# Revit family: Zumtobel CAELA
name_source: partatom
category: Lighting Fixtures
revit_build: Autodesk Revit 2018 (Build: 20170223_1515(x64)
units: mm (PartAtom-declared; Revit-internal decimal feet)

## family parameters
Cut with Voids When Loaded = No
Host = Face
Light Source = Yes
OmniClass Number = 23.80.70.11
OmniClass Title = Luminaries for Internal Lighting
Part Type = Normal
Room Calculation Point = No
Round Connector Dimension = Use Diameter
Shared = No

## types (4) — shared parameters
Assembly Code = D5020200
Color Filter = 16777215
Dimming Lamp Color Temperature Shift = <None>
Emit Shape Visible in Rendering = No
Height = 57 mm  [stored 0.187008 ft]
Lamp = LED
Manufacturer = Zumtobel Lighting
Tilt Angle = -90.00°
URL = http://www.zumtobel.com
zero-valued in all types: Default Elevation

## per-type parameters (varying)
| type | Apparent Load | Description | Emit from Circle Diameter | Interior Width | Length | Model | Photometric Web File | Round Shape | Square Shape | Width |
| CAELA QLS 431 | 18 VA | Square LED wall and ceiling luminaire | 431 mm  [stored 1.41404 ft] | 411 mm  [stored 1.34843 ft] | 431 mm  [stored 1.41404 ft] | 60815994 | ST8099.IES | No | Yes | 431 mm  [stored 1.41404 ft] |
| CAELA RMS LED1100-930 OP WH | 19 VA | Square LED wall and ceiling luminaire | 334 mm  [stored 1.0958 ft] | 314 mm  [stored 1.03018 ft] | 334 mm  [stored 1.0958 ft] | 60819086 | 60819068_(STD_LEO).IES | Yes | No | 334 mm  [stored 1.0958 ft] |
| CAELA RLS 432 | 23 VA | Round LED wall and ceiling luminaire | 432 mm  [stored 1.41732 ft] | 412 mm  [stored 1.35171 ft] | 432 mm  [stored 1.41732 ft] | 60815988 | ST8093.IES | Yes | No | 432 mm  [stored 1.41732 ft] |
| CAELA RMS 334 | 17 VA | Round LED wall and ceiling luminaire | 334 mm  [stored 1.0958 ft] | 314 mm  [stored 1.03018 ft] | 334 mm  [stored 1.0958 ft] | 60815976 | ST8090.IES | Yes | No | 334 mm  [stored 1.0958 ft] |

note: [stored X ft] marks values corroborated as IEEE doubles in the binary element streams (Revit-internal decimal feet)

## geometry (parser evidence)
native form markers: Blend x10, Sweep x3
no freeform markers — native parametric forms only
